# Revit family: P200921MX-002c_MBF2258FEZ
name_source: partatom
category: Specialty Equipment
units: mm (PartAtom-declared; Revit-internal decimal feet)

## family parameters
Always vertical = Yes
Cut with Voids When Loaded = No
Enable Cutting in Views = No
Maintain Annotation Orientation = No
Part Type = Normal
Room Calculation Point = No
Round Connector Dimension = Use Diameter
Shared = No
Work Plane-Based = No

## types (1)
- MBF2258FEZ
    Accent Material = ARCAT - Metal - Steel -Gray
    Amps = 0 A
    Body Material = ARCAT - Metal - Steel -Gray
    Clearance Material = ARCAT - Clearance
    Default Elevation = 0"
    Depth = 33 3/8"
    Description = 33-Inch Wide Bottom Mount Refrigerator - 22 Cu. Ft.
Réfrigérateur à portes françaises Maytag® à congélateur inférieur, 33 po, 22 pi3
    Dimension Guide = http://www.whirlpool.com
http://www.whirlpool.com
    Door Material = ARCAT - Metal - Steel - Stainless
    Energy Guide = https://www.maytag.com
http://access.whirlpool.com Guide&sku=MBF2258FEZ&language=FR
    Family Name = Refrigeration
    Feature 1 = Fingerprint Resistant Stainless Steel
Acier inoxydable résistant aux traces de doigts
    Feature 2 = BrightSeries™ LED Lighting
Éclairage BrightSeries™ à DEL
    Feature 3 = 10-Year Limited Parts Warranty on the Compressor
Garantie limitée de 10 ans sur les pièces du compresseur
    Handel Material = ARCAT - Metal - Steel -Gray - Light
    Height = 70"
    Logo Material = Stainless Steel
    Manufacturer = Maytag
    Model = MBF2258FEZ
    Type Image = <None>
    Voltage = 0 V
    Width = 32 5/8"

## geometry (parser evidence)
native form markers: Sweep x3
no freeform markers — native parametric forms only
